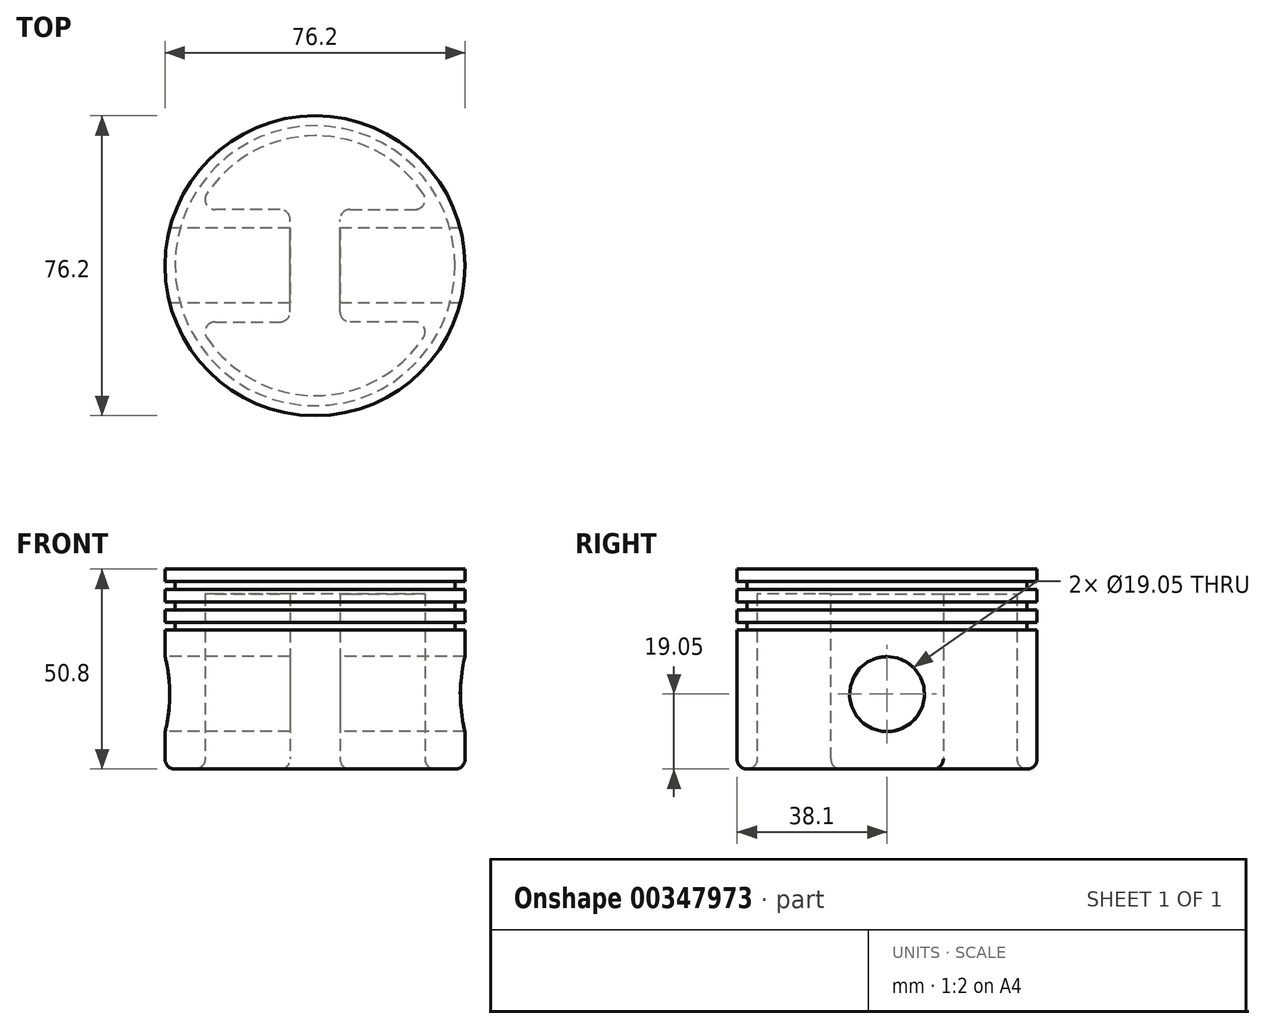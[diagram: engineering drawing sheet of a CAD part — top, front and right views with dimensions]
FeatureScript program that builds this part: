
annotation { "Feature Type Name" : "Feature", "Feature Type Description" : "" }
export const myFeature = defineFeature(function(context is Context, id is Id, definition is map)
    precondition{}
    {
        {
            var Q0;
            Q0=qCreatedBy(makeId("Top.planeOp"),FACE);
            var sketch = newSketch(context, id + "F0", { "sketchPlane" : qUnion([Q0])});
            skCircle(sketch, "E0", {"center": v(0, 0) * mm, "radius": 38.1 * mm});
            skSolve(sketch);
        }
        {
            var Q0;
            Q0 = qSketchRegion(id + "F0", true);
            extrude(context, id + "F1", {"entities" : qUnion([Q0]), "depth" : 50.8 * mm});
        }
        {
            var Q0;
            Q0=qCreatedBy(makeId("Right.planeOp"),FACE);
            cPlane(context, id + "F2", {"entities" : qUnion([Q0]), "cplaneType" : CPlaneType.OFFSET, "offset" : 38.1 * mm, "oppositeDirection" : true, "width" : 152.4 * mm, "height" : 152.4 * mm});
        }
        {
            var Q0;
            Q0=qCreatedBy(id+"F2.planeOp",FACE);
            var sketch = newSketch(context, id + "F3", { "sketchPlane" : qUnion([Q0])});
            skCircle(sketch, "E1", {"center": v(0, 19.05) * mm, "radius": 9.53 * mm});
            skSolve(sketch);
        }
        {
            var Q0;
            Q0 = qSketchRegion(id + "F3", true);
            extrude(context, id + "F4", {"entities" : qUnion([Q0]), "operationType" : NewBodyOperationType.REMOVE, "depth" : 76.2 * mm});
        }
        {
            var Q0;
            Q0=makeQuery(id+"F1.opExtrude","CAP_FACE",FACE,{"disambiguationData":[OSD([sQuery(id+"F0.wireOp",EDGE,"E0")])],"isStart":true});
            var sketch = newSketch(context, id + "F5", { "sketchPlane" : qUnion([Q0])});
            skArc(sketch, "E2", {"start": v(29.77, 14.29) * mm, "mid": v(0, 33.02) * mm, "end": v(-29.77, 14.29) * mm});
            skArc(sketch, "E3.trimOffspring", {"start": v(-29.77, -14.29) * mm, "mid": v(0, -33.02) * mm, "end": v(29.77, -14.29) * mm});
            skLineSegment(sketch, "E4", {"start": v(-29.77, 14.29) * mm, "end": v(-6.35, 14.29) * mm});
            skLineSegment(sketch, "E5", {"start": v(-6.35, 14.29) * mm, "end": v(-6.35, -14.29) * mm});
            skLineSegment(sketch, "E6", {"start": v(-6.35, -14.29) * mm, "end": v(-29.77, -14.29) * mm});
            skLineSegment(sketch, "E7", {"start": v(29.77, 14.29) * mm, "end": v(6.35, 14.29) * mm});
            skLineSegment(sketch, "E8", {"start": v(6.35, 14.29) * mm, "end": v(6.35, -14.29) * mm});
            skLineSegment(sketch, "E9", {"start": v(6.35, -14.29) * mm, "end": v(29.77, -14.29) * mm});
            skSolve(sketch);
        }
        {
            var Q0;
            Q0 = qSketchRegion(id + "F5", true);
            extrude(context, id + "F6", {"entities" : qUnion([Q0]), "operationType" : NewBodyOperationType.REMOVE, "oppositeDirection" : true, "depth" : 44.45 * mm});
        }
        {
            var Q0;
            Q0=qCreatedBy(makeId("Right.planeOp"),FACE);
            var sketch = newSketch(context, id + "F7", { "sketchPlane" : qUnion([Q0])});
            skLineSegment(sketch, "E10.bottom", {"start": v(-38.1, 35.33) * mm, "end": v(-35.56, 35.33) * mm});
            skLineSegment(sketch, "E10.top", {"start": v(-38.1, 37.31) * mm, "end": v(-35.56, 37.31) * mm});
            skLineSegment(sketch, "E10.left", {"start": v(-38.1, 35.33) * mm, "end": v(-38.1, 37.31) * mm});
            skLineSegment(sketch, "E10.right", {"start": v(-35.56, 35.33) * mm, "end": v(-35.56, 37.31) * mm});
            skLineSegment(sketch, "E11.bottom", {"start": v(-38.1, 40.49) * mm, "end": v(-35.56, 40.49) * mm});
            skLineSegment(sketch, "E11.top", {"start": v(-38.1, 42.47) * mm, "end": v(-35.56, 42.47) * mm});
            skLineSegment(sketch, "E11.left", {"start": v(-38.1, 40.49) * mm, "end": v(-38.1, 42.47) * mm});
            skLineSegment(sketch, "E11.right", {"start": v(-35.56, 40.49) * mm, "end": v(-35.56, 42.47) * mm});
            skLineSegment(sketch, "E12.bottom", {"start": v(-38.1, 45.64) * mm, "end": v(-35.56, 45.64) * mm});
            skLineSegment(sketch, "E12.top", {"start": v(-38.1, 47.63) * mm, "end": v(-35.56, 47.63) * mm});
            skLineSegment(sketch, "E12.left", {"start": v(-38.1, 45.64) * mm, "end": v(-38.1, 47.63) * mm});
            skLineSegment(sketch, "E12.right", {"start": v(-35.56, 45.64) * mm, "end": v(-35.56, 47.63) * mm});
            skSolve(sketch);
        }
        {
            var Q0;
            Q0 = qSketchRegion(id + "F7", true);
            var Q1;
            Q1=makeQuery(id+"F1.opExtrude","SWEPT_FACE",FACE,{"disambiguationData":[OSD([sQuery(id+"F0.wireOp",EDGE,"E0")])]});
            revolve(context, id + "F8", {"operationType" : NewBodyOperationType.REMOVE, "entities" : qUnion([Q0]), "axis" : qUnion([Q1]), "revolveType" : RevolveType.FULL, "oppositeDirection" : true});
        }
        {
            var Q0;
            Q0=makeQuery(id+"F6.boolean.opBoolean","COPY",EDGE,{"derivedFrom":makeQuery(id+"F6.opExtrude","SWEPT_EDGE",EDGE,{"disambiguationData":[OSD([sQuery(id+"F5.wireOp",EDGE,"E2"),sQuery(id+"F5.wireOp",EDGE,"E4")])]})});
            var Q1;
            Q1=makeQuery(id+"F6.boolean.opBoolean","COPY",EDGE,{"derivedFrom":makeQuery(id+"F6.opExtrude","SWEPT_EDGE",EDGE,{"disambiguationData":[OSD([sQuery(id+"F5.wireOp",EDGE,"E4"),sQuery(id+"F5.wireOp",EDGE,"E5")])]})});
            var Q2;
            Q2=makeQuery(id+"F6.boolean.opBoolean","COPY",EDGE,{"derivedFrom":makeQuery(id+"F6.opExtrude","SWEPT_EDGE",EDGE,{"disambiguationData":[OSD([sQuery(id+"F5.wireOp",EDGE,"E5"),sQuery(id+"F5.wireOp",EDGE,"E6")])]})});
            var Q3;
            Q3=makeQuery(id+"F6.boolean.opBoolean","COPY",EDGE,{"derivedFrom":makeQuery(id+"F6.opExtrude","SWEPT_EDGE",EDGE,{"disambiguationData":[OSD([sQuery(id+"F5.wireOp",EDGE,"E8"),sQuery(id+"F5.wireOp",EDGE,"E9")])]})});
            var Q4;
            Q4=makeQuery(id+"F6.boolean.opBoolean","COPY",EDGE,{"derivedFrom":makeQuery(id+"F6.opExtrude","SWEPT_EDGE",EDGE,{"disambiguationData":[OSD([sQuery(id+"F5.wireOp",EDGE,"E7"),sQuery(id+"F5.wireOp",EDGE,"E8")])]})});
            var Q5;
            Q5=makeQuery(id+"F6.boolean.opBoolean","COPY",EDGE,{"derivedFrom":makeQuery(id+"F6.opExtrude","SWEPT_EDGE",EDGE,{"disambiguationData":[OSD([sQuery(id+"F5.wireOp",EDGE,"E3.trimOffspring"),sQuery(id+"F5.wireOp",EDGE,"E9")])]})});
            var Q6;
            Q6=makeQuery(id+"F6.boolean.opBoolean","COPY",EDGE,{"derivedFrom":makeQuery(id+"F6.opExtrude","SWEPT_EDGE",EDGE,{"disambiguationData":[OSD([sQuery(id+"F5.wireOp",EDGE,"E2"),sQuery(id+"F5.wireOp",EDGE,"E7")])]})});
            var Q7;
            Q7=makeQuery(id+"F6.boolean.opBoolean","COPY",EDGE,{"derivedFrom":makeQuery(id+"F6.opExtrude","SWEPT_EDGE",EDGE,{"disambiguationData":[OSD([sQuery(id+"F5.wireOp",EDGE,"E3.trimOffspring"),sQuery(id+"F5.wireOp",EDGE,"E6")])]})});
            fillet(context, id + "F9", {"entities" : qUnion([Q0, Q1, Q2, Q3, Q4, Q5, Q6, Q7]), "radius" : 2.54 * mm, "tangentPropagation" : true, "allowEdgeOverflow" : false});
        }
        {
            var Q0;
            Q0=makeQuery(id+"F1.opExtrude","CAP_FACE",FACE,{"disambiguationData":[OSD([sQuery(id+"F0.wireOp",EDGE,"E0")])],"isStart":true});
            fillet(context, id + "F10", {"entities" : qUnion([Q0]), "radius" : 2.54 * mm, "tangentPropagation" : true, "allowEdgeOverflow" : false});
        }
    });
